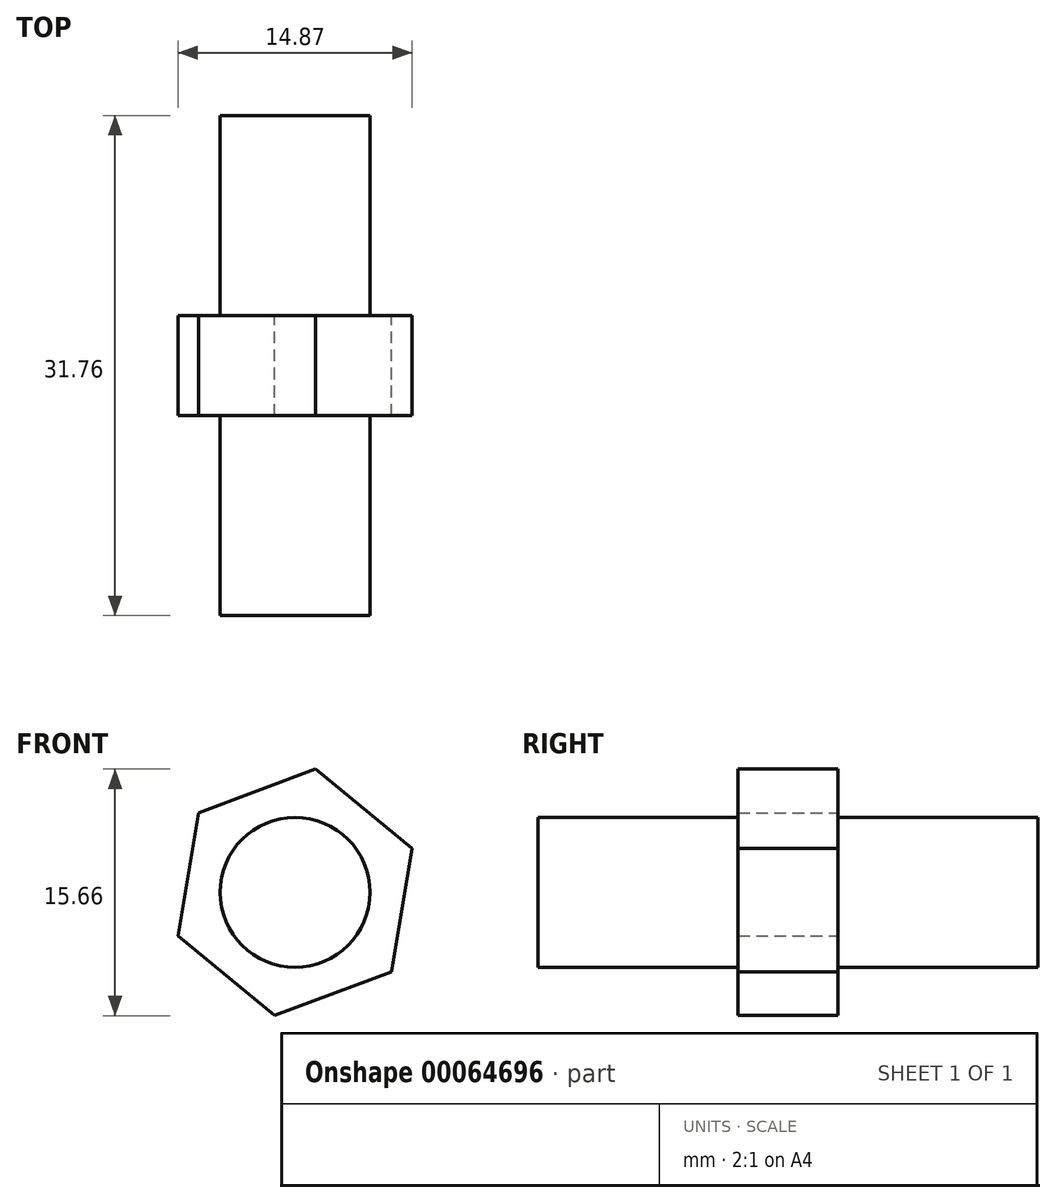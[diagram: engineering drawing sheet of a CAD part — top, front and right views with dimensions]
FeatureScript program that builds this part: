
annotation { "Feature Type Name" : "Feature", "Feature Type Description" : "" }
export const myFeature = defineFeature(function(context is Context, id is Id, definition is map)
    precondition{}
    {
        {
            var Q0;
            Q0=qCreatedBy(makeId("Front.planeOp"),FACE);
            var sketch = newSketch(context, id + "F0", { "sketchPlane" : qUnion([Q0])});
            skCircle(sketch, "E0.cCircle", {"center": v(-5.03, 0.35) * mm, "radius": 15.88 * mm, "construction": true});
            skLineSegment(sketch, "E0.0", {"start": v(9.84, 5.9) * mm, "end": v(7.21, -9.76) * mm});
            skLineSegment(sketch, "E0.1", {"start": v(7.21, -9.76) * mm, "end": v(-7.66, -15.31) * mm});
            skLineSegment(sketch, "E0.2", {"start": v(-7.66, -15.31) * mm, "end": v(-19.9, -5.2) * mm});
            skLineSegment(sketch, "E0.3", {"start": v(-19.9, -5.2) * mm, "end": v(-17.28, 10.45) * mm});
            skLineSegment(sketch, "E0.4", {"start": v(-17.28, 10.45) * mm, "end": v(-2.4, 16) * mm});
            skLineSegment(sketch, "E0.5", {"start": v(-2.4, 16) * mm, "end": v(9.84, 5.9) * mm});
            skSolve(sketch);
        }
        {
            var Q0;
            Q0 = qSketchRegion(id + "F0", true);
            extrude(context, id + "F1", {"entities" : qUnion([Q0]), "depth" : 6.35 * mm});
        }
        {
            var Q0;
            Q0=makeQuery(id+"F1.opExtrude","CAP_FACE",FACE,{"disambiguationData":[OSD([sQuery(id+"F0.wireOp",EDGE,"E0.0"),sQuery(id+"F0.wireOp",EDGE,"E0.1"),sQuery(id+"F0.wireOp",EDGE,"E0.2"),sQuery(id+"F0.wireOp",EDGE,"E0.3"),sQuery(id+"F0.wireOp",EDGE,"E0.4"),sQuery(id+"F0.wireOp",EDGE,"E0.5")])],"isStart":false});
            var sketch = newSketch(context, id + "F2", { "sketchPlane" : qUnion([Q0])});
            skCircle(sketch, "E1", {"center": v(-5.03, 0.35) * mm, "radius": 9.53 * mm});
            skSolve(sketch);
        }
        {
            var Q0;
            Q0 = qSketchRegion(id + "F2", true);
            extrude(context, id + "F3", {"entities" : qUnion([Q0]), "operationType" : NewBodyOperationType.ADD, "depth" : 25.4 * mm});
        }
        {
            var Q0;
            Q0=makeQuery(id+"F1.opExtrude","SWEPT_BODY",BODY,{"disambiguationData":[OSD([sQuery(id+"F0.wireOp",EDGE,"E0.0"),sQuery(id+"F0.wireOp",EDGE,"E0.1"),sQuery(id+"F0.wireOp",EDGE,"E0.2"),sQuery(id+"F0.wireOp",EDGE,"E0.3"),sQuery(id+"F0.wireOp",EDGE,"E0.4"),sQuery(id+"F0.wireOp",EDGE,"E0.5")])]});
            var Q1;
            Q1=makeQuery(id+"F1.opExtrude","CAP_FACE",FACE,{"disambiguationData":[OSD([sQuery(id+"F0.wireOp",EDGE,"E0.0"),sQuery(id+"F0.wireOp",EDGE,"E0.1"),sQuery(id+"F0.wireOp",EDGE,"E0.2"),sQuery(id+"F0.wireOp",EDGE,"E0.3"),sQuery(id+"F0.wireOp",EDGE,"E0.4"),sQuery(id+"F0.wireOp",EDGE,"E0.5")])],"isStart":true});
            mirror(context, id + "F4", {"operationType" : NewBodyOperationType.ADD, "entities" : qUnion([Q0]), "mirrorPlane" : qUnion([Q1])});
        }
        {
            var Q0;
            Q0=makeQuery(id+"F1.opExtrude","SWEPT_BODY",BODY,{"disambiguationData":[OSD([sQuery(id+"F0.wireOp",EDGE,"E0.0"),sQuery(id+"F0.wireOp",EDGE,"E0.1"),sQuery(id+"F0.wireOp",EDGE,"E0.2"),sQuery(id+"F0.wireOp",EDGE,"E0.3"),sQuery(id+"F0.wireOp",EDGE,"E0.4"),sQuery(id+"F0.wireOp",EDGE,"E0.5")])]});
            var Q1;
            Q1=qCreatedBy(makeId("Origin.pointOp"),VERTEX);
            transform(context, id + "F5", {"entities" : qUnion([Q0]), "transformType" : TransformType.SCALE_UNIFORMLY, "scale" : .5, "scalePoint" : qUnion([Q1]), "makeCopy" : false});
        }
    });
